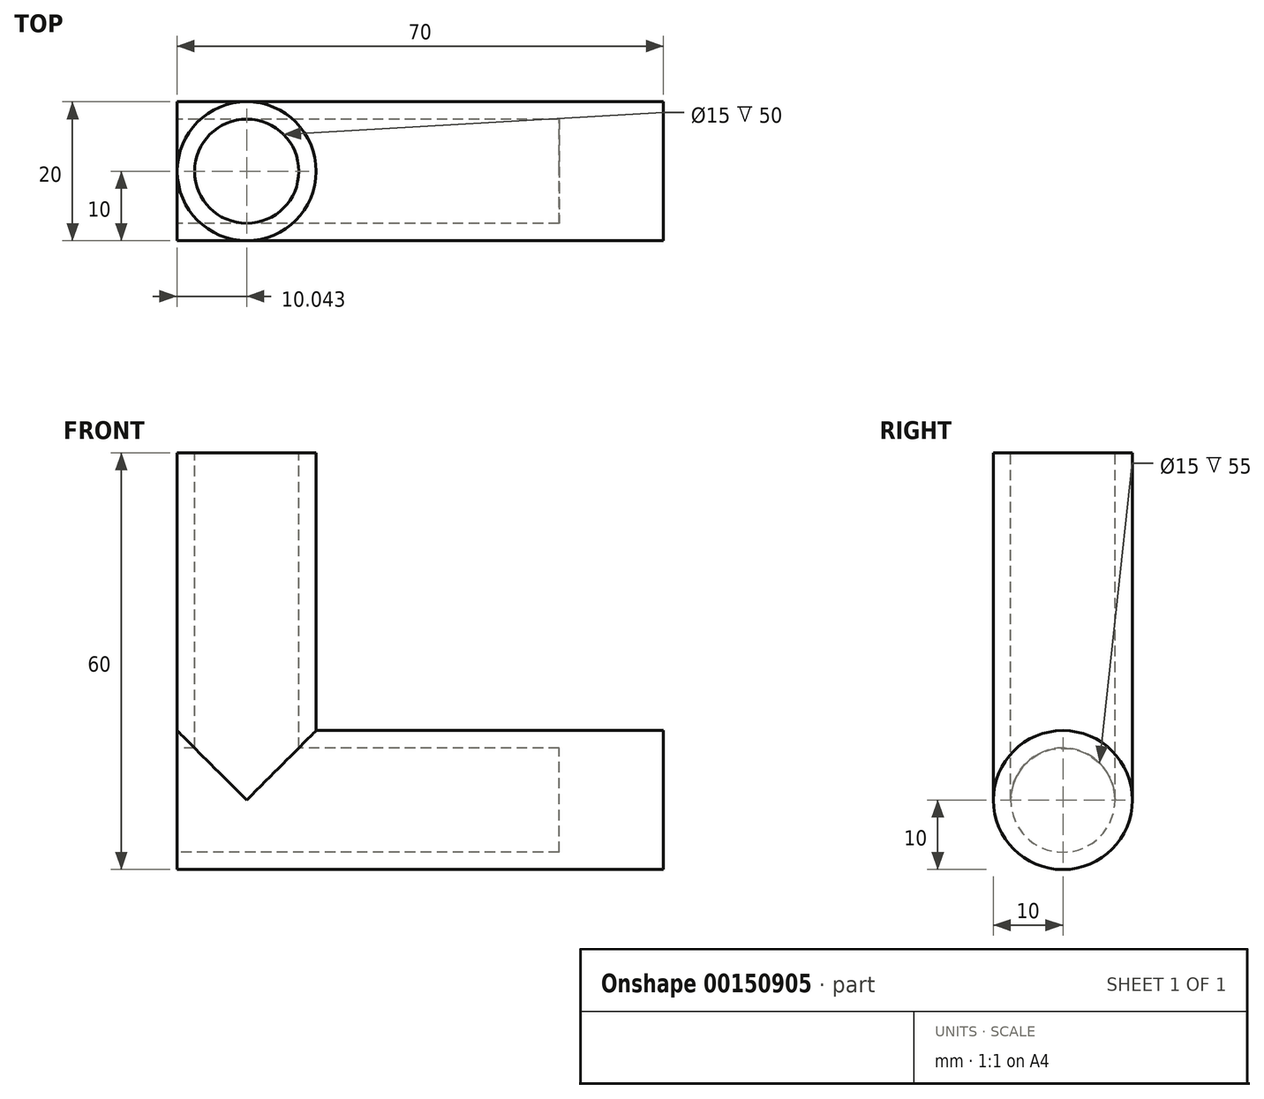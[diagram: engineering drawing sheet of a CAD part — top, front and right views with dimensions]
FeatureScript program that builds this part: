
annotation { "Feature Type Name" : "Feature", "Feature Type Description" : "" }
export const myFeature = defineFeature(function(context is Context, id is Id, definition is map)
    precondition{}
    {
        {
            var Q0;
            Q0=qCreatedBy(makeId("Top.planeOp"),FACE);
            var sketch = newSketch(context, id + "F0", { "sketchPlane" : qUnion([Q0])});
            skCircle(sketch, "E0", {"center": v(-9.96, 0) * mm, "radius": 10 * mm});
            skSolve(sketch);
        }
        {
            var Q0;
            Q0=makeQuery(id+"F0.imprint","IMPRINT",FACE,{"disambiguationData":[TD([[makeQuery(id+"F0.imprint","IMPRINT",EDGE,{"derivedFrom":sQuery(id+"F0.wireOp",EDGE,"E0")}),1.0]])]});
            extrude(context, id + "F1", {"entities" : qUnion([Q0]), "depth" : 40 * mm, "hasSecondDirection" : true, "secondDirectionOppositeDirection" : true, "secondDirectionDepth" : 10 * mm});
        }
        {
            var Q0;
            Q0=qCreatedBy(makeId("Right.planeOp"),FACE);
            var sketch = newSketch(context, id + "F2", { "sketchPlane" : qUnion([Q0])});
            skCircle(sketch, "E1", {"center": v(0, -10) * mm, "radius": 10 * mm});
            skSolve(sketch);
        }
        {
            var Q0;
            Q0 = qSketchRegion(id + "F2", true);
            var Q1;
            Q1=sQuery(id+"F2.wireOp",EDGE,"E1");
            extrude(context, id + "F3", {"entities" : qUnion([Q0]), "operationType" : NewBodyOperationType.ADD, "surfaceEntities" : qUnion([Q1]), "depth" : 50 * mm, "hasSecondDirection" : true, "secondDirectionOppositeDirection" : true, "secondDirectionDepth" : 20 * mm});
        }
        {
            var Q0;
            Q0=qCreatedBy(makeId("Right.planeOp"),FACE);
            var sketch = newSketch(context, id + "F4", { "sketchPlane" : qUnion([Q0])});
            skCircle(sketch, "E2", {"center": v(0, -10) * mm, "radius": 7.5 * mm});
            skSolve(sketch);
        }
        {
            var Q0;
            Q0 = qSketchRegion(id + "F4", true);
            var Q1;
            Q1=sQuery(id+"F4.wireOp",EDGE,"E2");
            extrude(context, id + "F5", {"entities" : qUnion([Q0]), "operationType" : NewBodyOperationType.REMOVE, "surfaceEntities" : qUnion([Q1]), "depth" : 35 * mm, "hasSecondDirection" : true, "secondDirectionOppositeDirection" : true, "secondDirectionDepth" : 25 * mm});
        }
        {
            var Q0;
            Q0=makeQuery(id+"F1.opExtrude","CAP_FACE",FACE,{"disambiguationData":[OSD([sQuery(id+"F0.wireOp",EDGE,"E0")])],"isStart":false});
            var sketch = newSketch(context, id + "F6", { "sketchPlane" : qUnion([Q0])});
            skCircle(sketch, "E3", {"center": v(-9.96, 0) * mm, "radius": 7.5 * mm});
            skSolve(sketch);
        }
        {
            var Q0;
            Q0=makeQuery(id+"F6.imprint","IMPRINT",FACE,{"disambiguationData":[TD([[makeQuery(id+"F6.imprint","IMPRINT",EDGE,{"derivedFrom":sQuery(id+"F6.wireOp",EDGE,"E3")}),1.0]])]});
            var Q1;
            Q1=sQuery(id+"F6.wireOp",EDGE,"E3");
            extrude(context, id + "F7", {"entities" : qUnion([Q0]), "operationType" : NewBodyOperationType.REMOVE, "surfaceEntities" : qUnion([Q1]), "oppositeDirection" : true, "depth" : 50 * mm});
        }
    });
